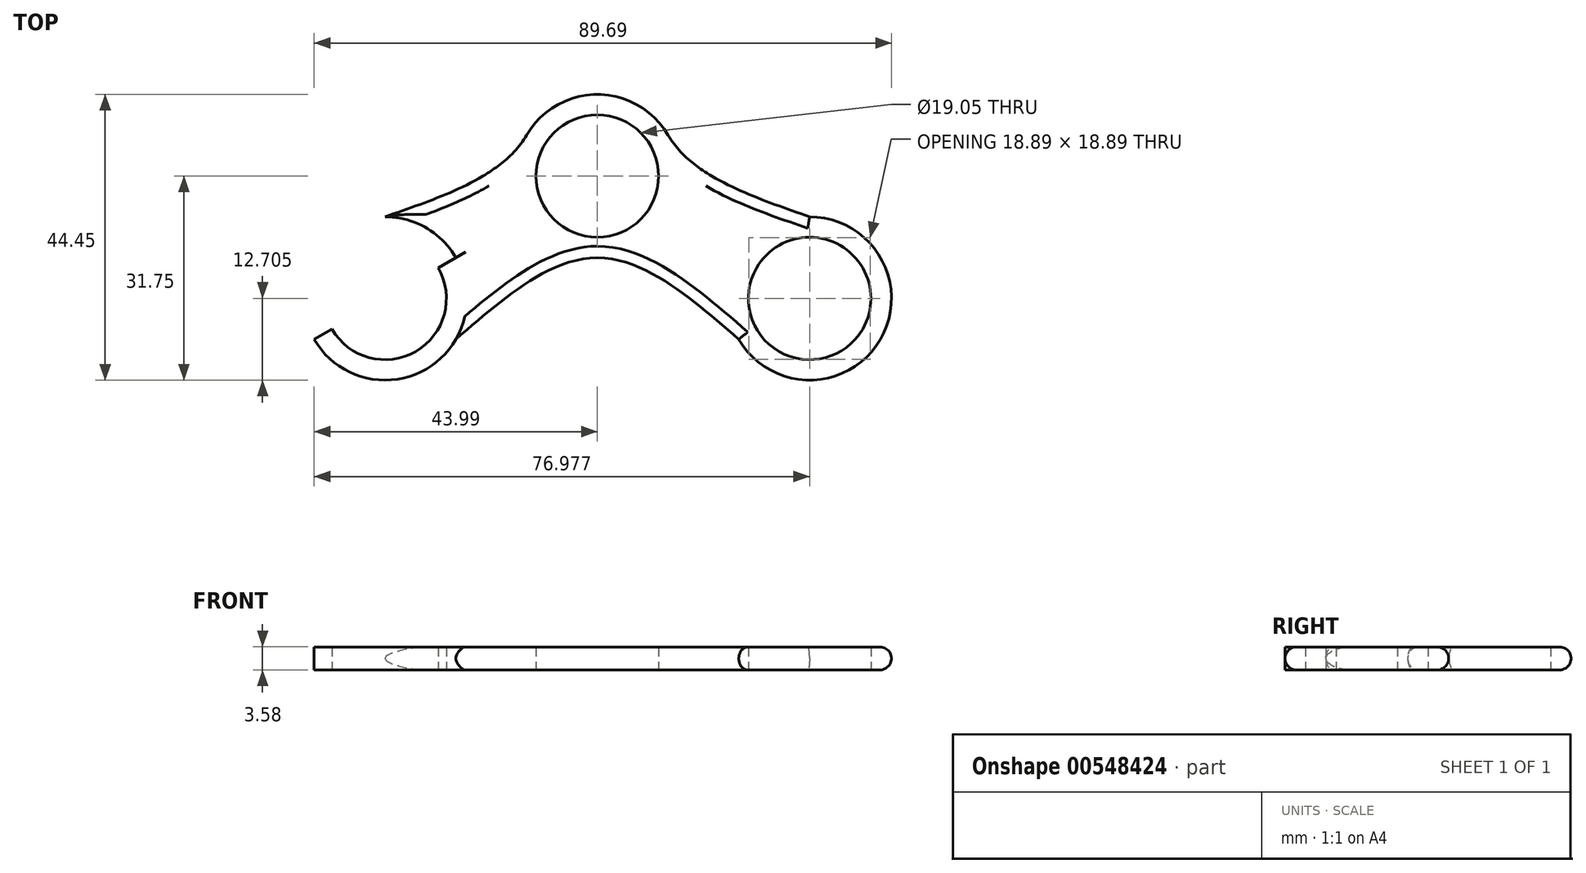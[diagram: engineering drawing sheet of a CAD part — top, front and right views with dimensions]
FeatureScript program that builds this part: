
annotation { "Feature Type Name" : "Feature", "Feature Type Description" : "" }
export const myFeature = defineFeature(function(context is Context, id is Id, definition is map)
    precondition{}
    {
        {
            var Q0;
            Q0=qCreatedBy(makeId("Top.planeOp"),FACE);
            var sketch = newSketch(context, id + "F0", { "sketchPlane" : qUnion([Q0])});
            skCircle(sketch, "E0", {"center": v(0, 0) * mm, "radius": 50.8 * mm});
            skLineSegment(sketch, "E1", {"start": v(0, 0) * mm, "end": v(0, 50.8) * mm});
            skLineSegment(sketch, "E2", {"start": v(0, 0) * mm, "end": v(-50.8, 0) * mm});
            skLineSegment(sketch, "E3", {"start": v(0, 0) * mm, "end": v(50.8, 0) * mm});
            skLineSegment(sketch, "E4", {"start": v(0, 0) * mm, "end": v(0, -50.8) * mm});
            skLineSegment(sketch, "E5", {"start": v(0, 0) * mm, "end": v(0, 38.09) * mm});
            skCircle(sketch, "E6", {"center": v(0, 38.09) * mm, "radius": 12.71 * mm});
            skCircle(sketch, "E7", {"center": v(0, 38.09) * mm, "radius": 9.53 * mm});
            skArc(sketch, "E8", {"start": v(0, 50.8) * mm, "mid": v(-44, 25.4) * mm, "end": v(-44, -25.4) * mm});
            skPoint(sketch, "E9", {"position": v(-44, -25.4) * mm});
            skPoint(sketch, "E10", {"position": v(0, 50.8) * mm});
            skPoint(sketch, "E11.MirrorP", {"position": v(44, -25.4) * mm});
            skLineSegment(sketch, "E12", {"start": v(-44, -25.4) * mm, "end": v(0, 0) * mm});
            skLineSegment(sketch, "E13", {"start": v(0, 0) * mm, "end": v(44, -25.4) * mm});
            skCircle(sketch, "E14.MirrorC", {"center": v(-32.99, -19.04) * mm, "radius": 9.53 * mm});
            skCircle(sketch, "E15.MirrorC", {"center": v(-32.99, -19.04) * mm, "radius": 12.71 * mm});
            skCircle(sketch, "E16.MirrorC", {"center": v(32.99, -19.04) * mm, "radius": 9.53 * mm});
            skCircle(sketch, "E17.MirrorC", {"center": v(32.99, -19.04) * mm, "radius": 12.71 * mm});
            skCircle(sketch, "E18", {"center": v(0, 0) * mm, "radius": 9.53 * mm});
            skCircle(sketch, "E19", {"center": v(0, 0) * mm, "radius": 12.7 * mm});
            skArc(sketch, "E20", {"start": v(-44, -25.4) * mm, "mid": v(-45.26, -15.76) * mm, "end": v(-39.34, -8.04) * mm});
            skPoint(sketch, "E21", {"position": v(0, -12.7) * mm});
            skPoint(sketch, "E22.MirrorP", {"position": v(11, 6.35) * mm});
            skPoint(sketch, "E23.MirrorP", {"position": v(-11, 6.35) * mm});
            skArc(sketch, "E24", {"start": v(-44, -25.4) * mm, "mid": v(-44, -12.69) * mm, "end": v(-32.99, -6.33) * mm});
            skPoint(sketch, "E25", {"position": v(-32.99, -6.33) * mm});
            skPoint(sketch, "E26.MirrorP", {"position": v(32.99, -6.33) * mm});
            skPoint(sketch, "E27.MirrorP", {"position": v(-11, 31.73) * mm});
            skPoint(sketch, "E28.MirrorP", {"position": v(11, 31.73) * mm});
            skFitSpline(sketch, "E29", {"points": [v(-32.99, -6.33) * mm, v(-11, 6.35) * mm, v(-11, 31.73) * mm], "startDerivative": vector(54.98, 19.02) * mm, "endDerivative": vector(-11.02, 57.12) * mm});
            skFitSpline(sketch, "E30.MirrorCS", {"points": [v(32.99, -6.33) * mm, v(11, 6.35) * mm, v(11, 31.73) * mm], "startDerivative": vector(-54.98, 19.02) * mm, "endDerivative": vector(11.02, 57.12) * mm});
            skArc(sketch, "E31", {"start": v(44, -25.4) * mm, "mid": v(32.99, -31.75) * mm, "end": v(21.98, -25.4) * mm});
            skPoint(sketch, "E32", {"position": v(21.98, -25.4) * mm});
            skArc(sketch, "E33", {"start": v(-44, -25.4) * mm, "mid": v(-32.99, -31.75) * mm, "end": v(-21.98, -25.4) * mm});
            skPoint(sketch, "E34", {"position": v(-21.98, -25.4) * mm});
            skFitSpline(sketch, "E35", {"points": [v(-21.98, -25.4) * mm, v(0, -12.7) * mm, v(21.98, -25.4) * mm], "startDerivative": vector(43.96, 38.1) * mm, "endDerivative": vector(43.96, -38.1) * mm});
            skSolve(sketch);
        }
        {
            var Q0;
            {var subQ0=sQuery(id+"F0.wireOp",EDGE,"E15.MirrorC");var subQ1=sQuery(id+"F0.wireOp",EDGE,"E12");var subQ2=makeQuery(id+"F0.imprint","INTERSECT",VERTEX,{"derivedFrom":[subQ1,subQ0]});Q0=makeQuery(id+"F0.imprint","IMPRINT",FACE,{"disambiguationData":[TD([[makeQuery(id+"F0.imprint","IMPRINT",EDGE,{"disambiguationData":[TD([[subQ2,-1.0]])],"derivedFrom":subQ1}),-1.0]])]});}
            var Q1;
            {var subQ0=sQuery(id+"F0.wireOp",EDGE,"E19");var subQ1=sQuery(id+"F0.wireOp",EDGE,"E2");var subQ2=makeQuery(id+"F0.imprint","INTERSECT",VERTEX,{"derivedFrom":[subQ1,subQ0]});Q1=makeQuery(id+"F0.imprint","IMPRINT",FACE,{"disambiguationData":[TD([[makeQuery(id+"F0.imprint","IMPRINT",EDGE,{"disambiguationData":[TD([[subQ2,-1.0]])],"derivedFrom":subQ1}),1.0]])]});}
            var Q2;
            {var subQ0=sQuery(id+"F0.wireOp",EDGE,"E15.MirrorC");var subQ9=makeQuery(id+"F0.imprint","IMPRINT",VERTEX,{"derivedFrom":subQ0});Q2=makeQuery(id+"F0.imprint","IMPRINT",FACE,{"disambiguationData":[TD([[makeQuery(id+"F0.imprint","IMPRINT",EDGE,{"disambiguationData":[TD([[subQ9,1.0]])],"derivedFrom":subQ0}),-1.0]])]});}
            var Q3;
            {var subQ2=sQuery(id+"F0.wireOp",EDGE,"E12");var subQ4=sQuery(id+"F0.wireOp",EDGE,"E14.MirrorC");var subQ6=makeQuery(id+"F0.imprint","INTERSECT",VERTEX,{"disambiguationData":[OD(1.0)],"derivedFrom":[subQ2,subQ4]});Q3=makeQuery(id+"F0.imprint","IMPRINT",FACE,{"disambiguationData":[TD([[makeQuery(id+"F0.imprint","IMPRINT",EDGE,{"disambiguationData":[TD([[subQ6,-1.0]])],"derivedFrom":subQ2}),-1.0]])]});}
            var Q4;
            {var subQ0=sQuery(id+"F0.wireOp",EDGE,"E19");var subQ1=sQuery(id+"F0.wireOp",EDGE,"E2");var subQ2=makeQuery(id+"F0.imprint","INTERSECT",VERTEX,{"derivedFrom":[subQ1,subQ0]});Q4=makeQuery(id+"F0.imprint","IMPRINT",FACE,{"disambiguationData":[TD([[makeQuery(id+"F0.imprint","IMPRINT",EDGE,{"disambiguationData":[TD([[subQ2,-1.0]])],"derivedFrom":subQ1}),-1.0]])]});}
            var Q5;
            {var subQ0=sQuery(id+"F0.wireOp",EDGE,"E19");var subQ1=sQuery(id+"F0.wireOp",EDGE,"E5");var subQ2=makeQuery(id+"F0.imprint","INTERSECT",VERTEX,{"derivedFrom":[subQ1,subQ0]});Q5=makeQuery(id+"F0.imprint","IMPRINT",FACE,{"disambiguationData":[TD([[makeQuery(id+"F0.imprint","IMPRINT",EDGE,{"disambiguationData":[TD([[subQ2,-1.0]])],"derivedFrom":subQ1}),1.0]])]});}
            var Q6;
            {var subQ0=sQuery(id+"F0.wireOp",EDGE,"E6");var subQ2=sQuery(id+"F0.wireOp",EDGE,"E5");var subQ3=makeQuery(id+"F0.imprint","INTERSECT",VERTEX,{"derivedFrom":[subQ2,subQ0]});Q6=makeQuery(id+"F0.imprint","IMPRINT",FACE,{"disambiguationData":[TD([[makeQuery(id+"F0.imprint","IMPRINT",EDGE,{"disambiguationData":[TD([[subQ3,-1.0]])],"derivedFrom":subQ2}),1.0]])]});}
            var Q7;
            {var subQ0=sQuery(id+"F0.wireOp",EDGE,"E6");var subQ2=sQuery(id+"F0.wireOp",EDGE,"E5");var subQ3=makeQuery(id+"F0.imprint","INTERSECT",VERTEX,{"derivedFrom":[subQ2,subQ0]});Q7=makeQuery(id+"F0.imprint","IMPRINT",FACE,{"disambiguationData":[TD([[makeQuery(id+"F0.imprint","IMPRINT",EDGE,{"disambiguationData":[TD([[subQ3,-1.0]])],"derivedFrom":subQ2}),-1.0]])]});}
            var Q8;
            {var subQ0=sQuery(id+"F0.wireOp",EDGE,"E19");var subQ1=sQuery(id+"F0.wireOp",EDGE,"E5");var subQ2=makeQuery(id+"F0.imprint","INTERSECT",VERTEX,{"derivedFrom":[subQ1,subQ0]});Q8=makeQuery(id+"F0.imprint","IMPRINT",FACE,{"disambiguationData":[TD([[makeQuery(id+"F0.imprint","IMPRINT",EDGE,{"disambiguationData":[TD([[subQ2,-1.0]])],"derivedFrom":subQ1}),-1.0]])]});}
            var Q9;
            {var subQ0=sQuery(id+"F0.wireOp",EDGE,"E18");var subQ1=sQuery(id+"F0.wireOp",EDGE,"E3");var subQ2=makeQuery(id+"F0.imprint","INTERSECT",VERTEX,{"derivedFrom":[subQ1,subQ0]});Q9=makeQuery(id+"F0.imprint","IMPRINT",FACE,{"disambiguationData":[TD([[makeQuery(id+"F0.imprint","IMPRINT",EDGE,{"disambiguationData":[TD([[subQ2,-1.0]])],"derivedFrom":subQ1}),1.0]])]});}
            var Q10;
            {var subQ0=sQuery(id+"F0.wireOp",EDGE,"E18");var subQ1=sQuery(id+"F0.wireOp",EDGE,"E2");var subQ2=makeQuery(id+"F0.imprint","INTERSECT",VERTEX,{"derivedFrom":[subQ1,subQ0]});Q10=makeQuery(id+"F0.imprint","IMPRINT",FACE,{"disambiguationData":[TD([[makeQuery(id+"F0.imprint","IMPRINT",EDGE,{"disambiguationData":[TD([[subQ2,-1.0]])],"derivedFrom":subQ1}),-1.0]])]});}
            var Q11;
            {var subQ0=sQuery(id+"F0.wireOp",EDGE,"E18");var subQ1=sQuery(id+"F0.wireOp",EDGE,"E2");var subQ2=makeQuery(id+"F0.imprint","INTERSECT",VERTEX,{"derivedFrom":[subQ1,subQ0]});Q11=makeQuery(id+"F0.imprint","IMPRINT",FACE,{"disambiguationData":[TD([[makeQuery(id+"F0.imprint","IMPRINT",EDGE,{"disambiguationData":[TD([[subQ2,-1.0]])],"derivedFrom":subQ1}),1.0]])]});}
            var Q12;
            {var subQ3=sQuery(id+"F0.wireOp",EDGE,"E19");var subQ5=sQuery(id+"F0.wireOp",EDGE,"E12");var subQ6=makeQuery(id+"F0.imprint","INTERSECT",VERTEX,{"derivedFrom":[subQ5,subQ3]});Q12=makeQuery(id+"F0.imprint","IMPRINT",FACE,{"disambiguationData":[TD([[makeQuery(id+"F0.imprint","IMPRINT",EDGE,{"disambiguationData":[TD([[subQ6,-1.0]])],"derivedFrom":subQ5}),-1.0]])]});}
            var Q13;
            {var subQ0=sQuery(id+"F0.wireOp",EDGE,"E18");var subQ5=sQuery(id+"F0.wireOp",EDGE,"E13");var subQ6=makeQuery(id+"F0.imprint","INTERSECT",VERTEX,{"derivedFrom":[subQ5,subQ0]});Q13=makeQuery(id+"F0.imprint","IMPRINT",FACE,{"disambiguationData":[TD([[makeQuery(id+"F0.imprint","IMPRINT",EDGE,{"disambiguationData":[TD([[subQ6,-1.0]])],"derivedFrom":subQ5}),-1.0]])]});}
            var Q14;
            {var subQ0=sQuery(id+"F0.wireOp",EDGE,"E18");var subQ1=sQuery(id+"F0.wireOp",EDGE,"E3");var subQ2=makeQuery(id+"F0.imprint","INTERSECT",VERTEX,{"derivedFrom":[subQ1,subQ0]});Q14=makeQuery(id+"F0.imprint","IMPRINT",FACE,{"disambiguationData":[TD([[makeQuery(id+"F0.imprint","IMPRINT",EDGE,{"disambiguationData":[TD([[subQ2,-1.0]])],"derivedFrom":subQ1}),-1.0]])]});}
            var Q15;
            {var subQ0=sQuery(id+"F0.wireOp",EDGE,"E19");var subQ1=sQuery(id+"F0.wireOp",EDGE,"E3");var subQ2=makeQuery(id+"F0.imprint","INTERSECT",VERTEX,{"derivedFrom":[subQ1,subQ0]});Q15=makeQuery(id+"F0.imprint","IMPRINT",FACE,{"disambiguationData":[TD([[makeQuery(id+"F0.imprint","IMPRINT",EDGE,{"disambiguationData":[TD([[subQ2,-1.0]])],"derivedFrom":subQ1}),1.0]])]});}
            var Q16;
            {var subQ0=sQuery(id+"F0.wireOp",EDGE,"E19");var subQ1=sQuery(id+"F0.wireOp",EDGE,"E3");var subQ2=makeQuery(id+"F0.imprint","INTERSECT",VERTEX,{"derivedFrom":[subQ1,subQ0]});Q16=makeQuery(id+"F0.imprint","IMPRINT",FACE,{"disambiguationData":[TD([[makeQuery(id+"F0.imprint","IMPRINT",EDGE,{"disambiguationData":[TD([[subQ2,-1.0]])],"derivedFrom":subQ1}),-1.0]])]});}
            var Q17;
            {var subQ0=sQuery(id+"F0.wireOp",EDGE,"E19");var subQ1=sQuery(id+"F0.wireOp",EDGE,"E13");var subQ2=makeQuery(id+"F0.imprint","INTERSECT",VERTEX,{"derivedFrom":[subQ1,subQ0]});Q17=makeQuery(id+"F0.imprint","IMPRINT",FACE,{"disambiguationData":[TD([[makeQuery(id+"F0.imprint","IMPRINT",EDGE,{"disambiguationData":[TD([[subQ2,-1.0]])],"derivedFrom":subQ1}),-1.0]])]});}
            var Q18;
            {var subQ0=sQuery(id+"F0.wireOp",EDGE,"E17.MirrorC");var subQ1=sQuery(id+"F0.wireOp",EDGE,"E13");var subQ7=makeQuery(id+"F0.imprint","INTERSECT",VERTEX,{"derivedFrom":[subQ1,subQ0]});Q18=makeQuery(id+"F0.imprint","IMPRINT",FACE,{"disambiguationData":[TD([[makeQuery(id+"F0.imprint","IMPRINT",EDGE,{"disambiguationData":[TD([[subQ7,-1.0]])],"derivedFrom":subQ1}),-1.0]])]});}
            var Q19;
            {var subQ0=sQuery(id+"F0.wireOp",EDGE,"E17.MirrorC");var subQ1=sQuery(id+"F0.wireOp",EDGE,"E13");var subQ8=makeQuery(id+"F0.imprint","INTERSECT",VERTEX,{"derivedFrom":[subQ1,subQ0]});Q19=makeQuery(id+"F0.imprint","IMPRINT",FACE,{"disambiguationData":[TD([[makeQuery(id+"F0.imprint","IMPRINT",EDGE,{"disambiguationData":[TD([[subQ8,-1.0]])],"derivedFrom":subQ1}),1.0]])]});}
            extrude(context, id + "F1", {"entities" : qUnion([Q0, Q1, Q2, Q3, Q4, Q5, Q6, Q7, Q8, Q9, Q10, Q11, Q12, Q13, Q14, Q15, Q16, Q17, Q18, Q19]), "endBound" : BoundingType.SYMMETRIC, "depth" : 3.57 * mm, "offsetDistance" : 25.4 * mm});
        }
        {
            var Q0;
            Q0=makeQuery(id+"F1.opExtrude","CAP_EDGE",EDGE,{"disambiguationData":[OSD([sQuery(id+"F0.wireOp",EDGE,"E29")])],"isStart":false});
            var Q1;
            Q1=makeQuery(id+"F1.opExtrude","CAP_EDGE",EDGE,{"disambiguationData":[OSD([sQuery(id+"F0.wireOp",EDGE,"E30.MirrorCS")])],"isStart":false});
            var Q2;
            Q2=makeQuery(id+"F1.opExtrude","CAP_EDGE",EDGE,{"disambiguationData":[OSD([sQuery(id+"F0.wireOp",EDGE,"E6")])],"isStart":false});
            var Q3;
            Q3=makeQuery(id+"F1.opExtrude","CAP_EDGE",EDGE,{"disambiguationData":[OSD([sQuery(id+"F0.wireOp",EDGE,"E17.MirrorC")])],"isStart":false});
            var Q4;
            Q4=makeQuery(id+"F1.opExtrude","CAP_EDGE",EDGE,{"disambiguationData":[OSD([sQuery(id+"F0.wireOp",EDGE,"E35")])],"isStart":false});
            var Q5;
            Q5=makeQuery(id+"F1.opExtrude","CAP_EDGE",EDGE,{"disambiguationData":[OSD([sQuery(id+"F0.wireOp",EDGE,"E15.MirrorC")])],"isStart":false});
            fillet(context, id + "F2", {"entities" : qUnion([Q0, Q1, Q2, Q3, Q4, Q5]), "radius" : 1.79 * mm, "tangentPropagation" : true, "allowEdgeOverflow" : false});
        }
        {
            var Q0;
            Q0=makeQuery(id+"F1.opExtrude","CAP_EDGE",EDGE,{"disambiguationData":[OSD([sQuery(id+"F0.wireOp",EDGE,"E35")])],"isStart":true});
            var Q1;
            Q1=makeQuery(id+"F1.opExtrude","CAP_EDGE",EDGE,{"disambiguationData":[OSD([sQuery(id+"F0.wireOp",EDGE,"E15.MirrorC")])],"isStart":true});
            var Q2;
            Q2=makeQuery(id+"F1.opExtrude","CAP_EDGE",EDGE,{"disambiguationData":[OSD([sQuery(id+"F0.wireOp",EDGE,"E17.MirrorC")])],"isStart":true});
            var Q3;
            Q3=makeQuery(id+"F1.opExtrude","CAP_EDGE",EDGE,{"disambiguationData":[OSD([sQuery(id+"F0.wireOp",EDGE,"E30.MirrorCS")])],"isStart":true});
            var Q4;
            Q4=makeQuery(id+"F1.opExtrude","CAP_EDGE",EDGE,{"disambiguationData":[OSD([sQuery(id+"F0.wireOp",EDGE,"E29")])],"isStart":true});
            var Q5;
            Q5=makeQuery(id+"F1.opExtrude","CAP_EDGE",EDGE,{"disambiguationData":[OSD([sQuery(id+"F0.wireOp",EDGE,"E6")])],"isStart":true});
            fillet(context, id + "F3", {"entities" : qUnion([Q0, Q1, Q2, Q3, Q4, Q5]), "radius" : 1.79 * mm, "tangentPropagation" : true, "allowEdgeOverflow" : false});
        }
    });
